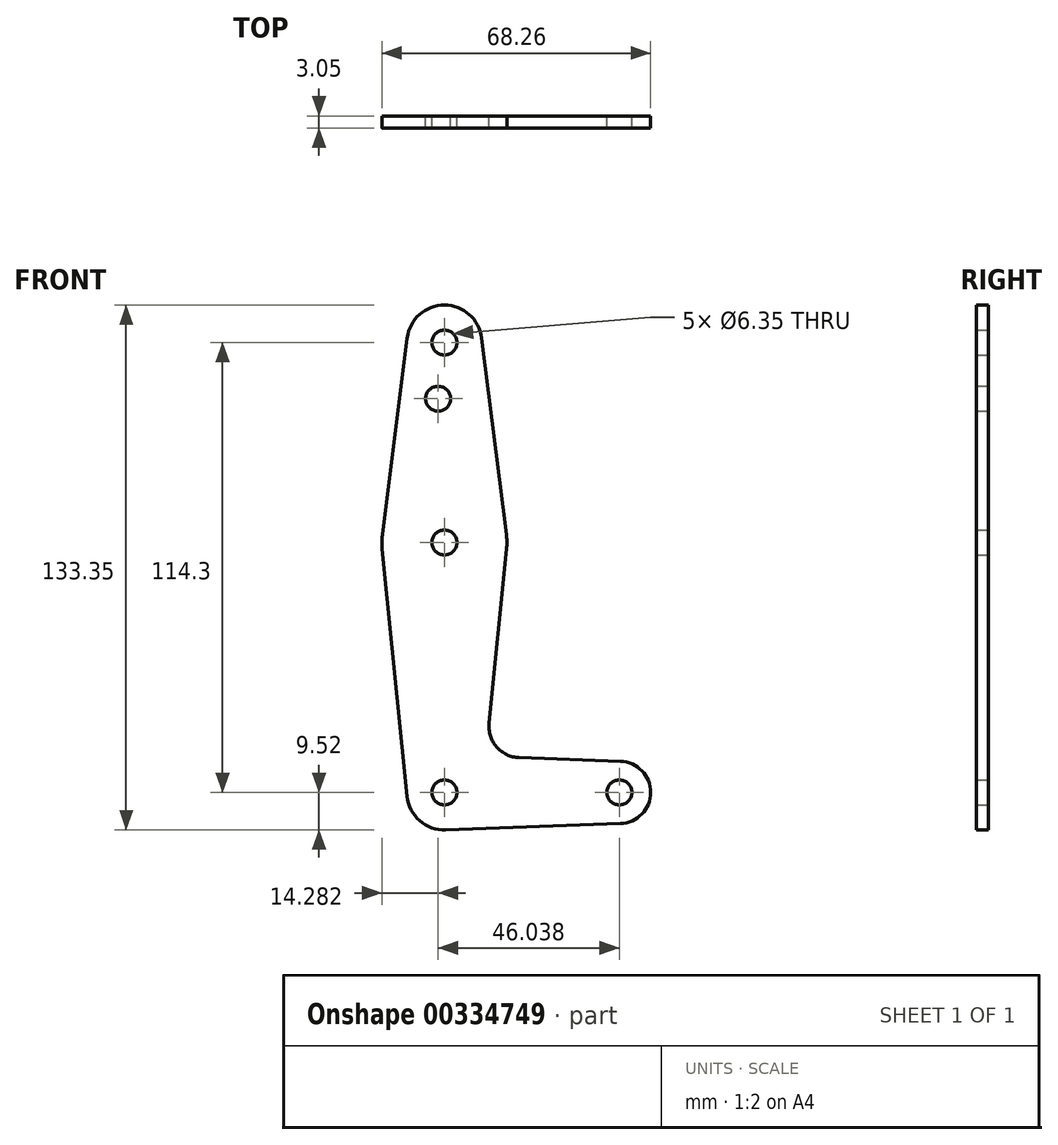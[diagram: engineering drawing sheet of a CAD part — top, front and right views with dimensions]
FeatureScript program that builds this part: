
annotation { "Feature Type Name" : "Feature", "Feature Type Description" : "" }
export const myFeature = defineFeature(function(context is Context, id is Id, definition is map)
    precondition{}
    {
        {
            var Q0;
            Q0=qCreatedBy(makeId("Front.planeOp"),FACE);
            var sketch = newSketch(context, id + "F0", { "sketchPlane" : qUnion([Q0])});
            skLineSegment(sketch, "E0", {"start": v(0, 0) * mm, "end": v(0, 114.3) * mm, "construction": true});
            skCircle(sketch, "E1", {"center": v(0, 0) * mm, "radius": 9.52 * mm});
            skCircle(sketch, "E2", {"center": v(0, 114.3) * mm, "radius": 9.52 * mm});
            skLineSegment(sketch, "E3", {"start": v(0, 0) * mm, "end": v(0, 57.15) * mm});
            skCircle(sketch, "E4", {"center": v(0, 63.5) * mm, "radius": 15.88 * mm});
            skLineSegment(sketch, "E5", {"start": v(-9.45, 115.5) * mm, "end": v(-15.75, 65.48) * mm});
            skLineSegment(sketch, "E6", {"start": v(9.45, 115.5) * mm, "end": v(15.75, 65.48) * mm});
            skCircle(sketch, "E7", {"center": v(0, 114.3) * mm, "radius": 3.18 * mm});
            skCircle(sketch, "E8", {"center": v(0, 63.5) * mm, "radius": 3.18 * mm});
            skCircle(sketch, "E9", {"center": v(0, 0) * mm, "radius": 3.18 * mm});
            skLineSegment(sketch, "E10", {"start": v(0, 0) * mm, "end": v(44.45, 0) * mm, "construction": true});
            skCircle(sketch, "E11", {"center": v(44.45, 0) * mm, "radius": 7.94 * mm});
            skCircle(sketch, "E12", {"center": v(44.45, 0) * mm, "radius": 3.18 * mm});
            skLineSegment(sketch, "E13", {"start": v(0.34, -9.52) * mm, "end": v(44.73, -7.93) * mm});
            skCircle(sketch, "E14", {"center": v(-1.59, 100.03) * mm, "radius": 3.18 * mm});
            skLineSegment(sketch, "E15", {"start": v(18.97, 8.85) * mm, "end": v(44.73, 7.93) * mm});
            skLineSegment(sketch, "E16", {"start": v(15.8, 61.91) * mm, "end": v(11.34, 17.6) * mm});
            skLineSegment(sketch, "E17", {"start": v(-15.8, 61.91) * mm, "end": v(-9.48, -0.95) * mm});
            skArc(sketch, "E18.filletArc", {"start": v(11.34, 17.6) * mm, "mid": v(13.26, 11.57) * mm, "end": v(18.97, 8.85) * mm});
            skSolve(sketch);
        }
        {
            var Q0;
            Q0 = qSketchRegion(id + "F0", true);
            extrude(context, id + "F1", {"entities" : qUnion([Q0]), "depth" : 3.05 * mm});
        }
    });
